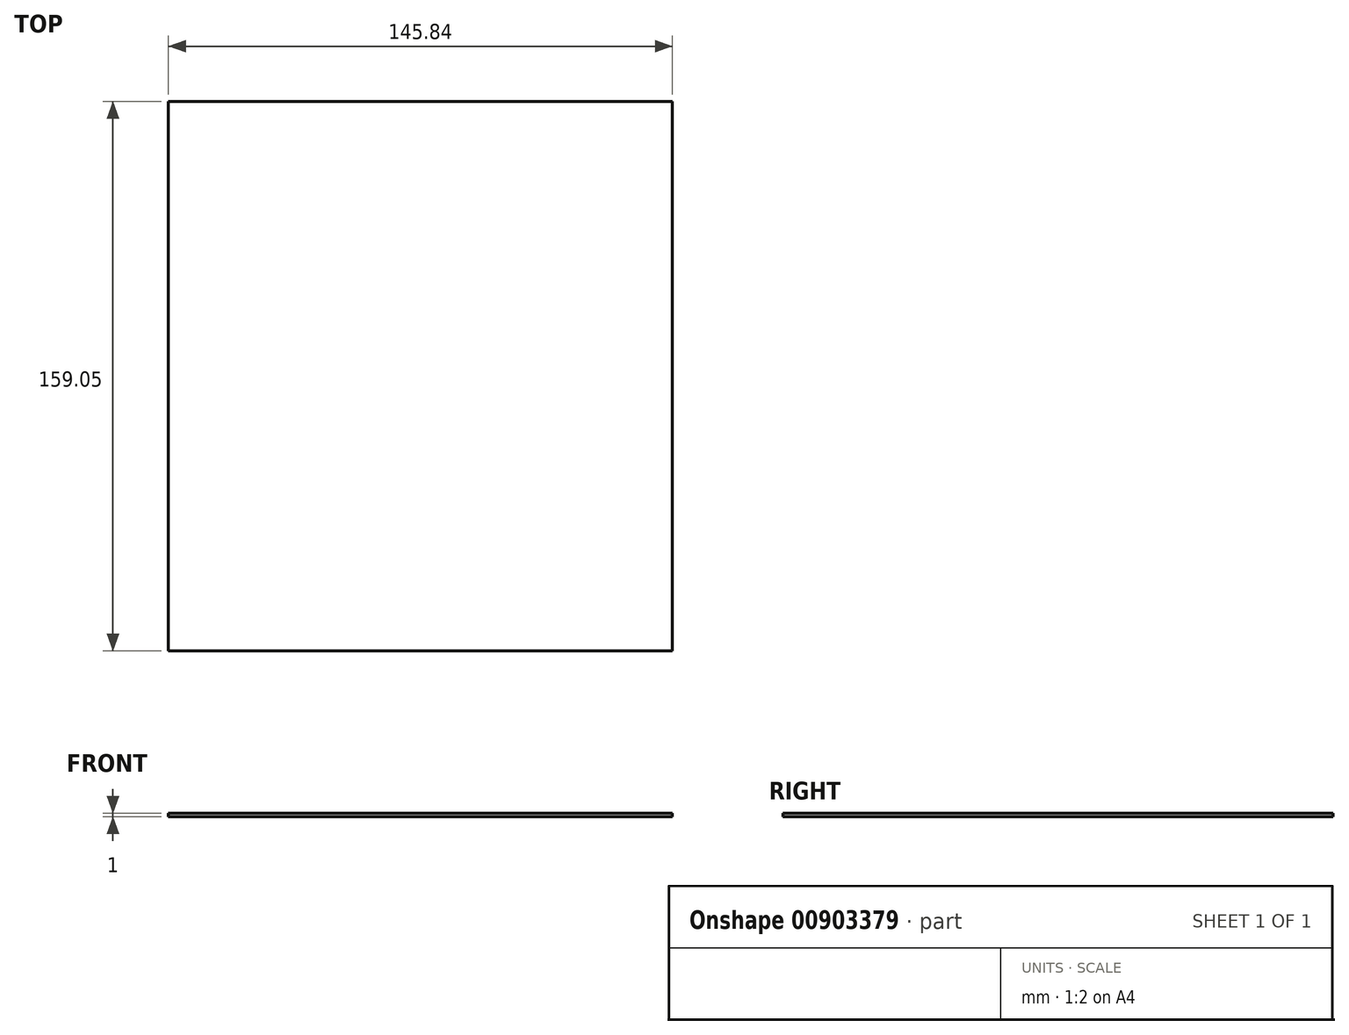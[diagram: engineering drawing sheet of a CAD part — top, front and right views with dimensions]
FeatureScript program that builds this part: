
annotation { "Feature Type Name" : "Feature", "Feature Type Description" : "" }
export const myFeature = defineFeature(function(context is Context, id is Id, definition is map)
    precondition{}
    {
        {
            var Q0;
            Q0=qCreatedBy(makeId("Top.planeOp"), FACE);
            var sketch = newSketch(context, id + "F0", { "sketchPlane" : qUnion([Q0])});
            skLineSegment(sketch, "E0.bottom", {"start": v(0, 0) * mm, "end": v(145.84, 0) * mm});
            skLineSegment(sketch, "E0.top", {"start": v(0, -159.05) * mm, "end": v(145.84, -159.05) * mm});
            skLineSegment(sketch, "E0.left", {"start": v(0, 0) * mm, "end": v(0, -159.05) * mm});
            skLineSegment(sketch, "E0.right", {"start": v(145.84, 0) * mm, "end": v(145.84, -159.05) * mm});
            skSolve(sketch);
        }
        {
            var Q0;
            Q0 = qSketchRegion(id + "F0", true);
            extrude(context, id + "F1", {"entities" : qUnion([Q0]), "depth" : 1 * mm, "offsetDistance" : 25 * mm});
        }
    });
